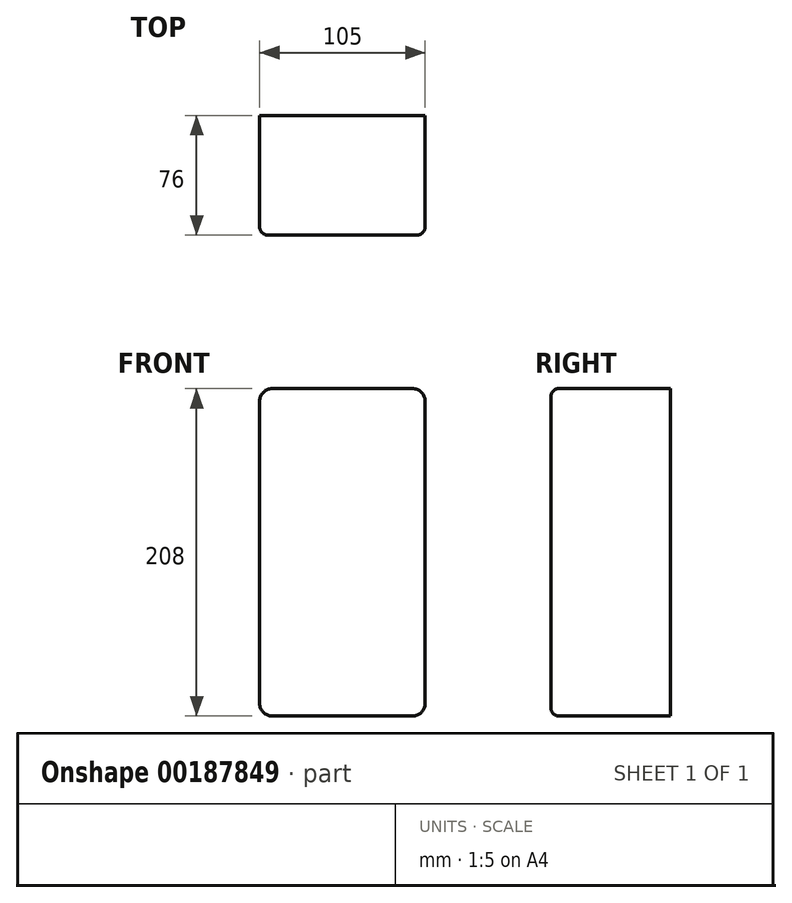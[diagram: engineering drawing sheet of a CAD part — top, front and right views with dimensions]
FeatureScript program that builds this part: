
annotation { "Feature Type Name" : "Feature", "Feature Type Description" : "" }
export const myFeature = defineFeature(function(context is Context, id is Id, definition is map)
    precondition{}
    {
        {
            var Q0;
            Q0=qCreatedBy(makeId("Front.planeOp"),FACE);
            var sketch = newSketch(context, id + "F0", { "sketchPlane" : qUnion([Q0])});
            skLineSegment(sketch, "E0.bottom", {"start": v(-13.11, 91.26) * mm, "end": v(75.89, 91.26) * mm});
            skLineSegment(sketch, "E0.top", {"start": v(-13.11, -116.74) * mm, "end": v(75.89, -116.74) * mm});
            skLineSegment(sketch, "E0.left", {"start": v(-21.11, 83.26) * mm, "end": v(-21.11, -108.74) * mm});
            skLineSegment(sketch, "E0.right", {"start": v(83.89, 83.26) * mm, "end": v(83.89, -108.74) * mm});
            skPoint(sketch, "E1.visualSharp", {"position": v(83.89, 91.26) * mm});
            skArc(sketch, "E1.filletArc", {"start": v(83.89, 83.26) * mm, "mid": v(81.54, 88.91) * mm, "end": v(75.89, 91.26) * mm});
            skPoint(sketch, "E2.visualSharp", {"position": v(-21.11, 91.26) * mm});
            skArc(sketch, "E2.filletArc", {"start": v(-13.11, 91.26) * mm, "mid": v(-18.77, 88.91) * mm, "end": v(-21.11, 83.26) * mm});
            skPoint(sketch, "E3.visualSharp", {"position": v(-21.11, -116.74) * mm});
            skArc(sketch, "E3.filletArc", {"start": v(-21.11, -108.74) * mm, "mid": v(-18.77, -114.4) * mm, "end": v(-13.11, -116.74) * mm});
            skPoint(sketch, "E4.visualSharp", {"position": v(83.89, -116.74) * mm});
            skArc(sketch, "E4.filletArc", {"start": v(75.89, -116.74) * mm, "mid": v(81.54, -114.4) * mm, "end": v(83.89, -108.74) * mm});
            skSolve(sketch);
        }
        {
            var Q0;
            Q0=makeQuery(id+"F0.imprint","IMPRINT",FACE,{"disambiguationData":[TD([[makeQuery(id+"F0.imprint","IMPRINT",EDGE,{"derivedFrom":sQuery(id+"F0.wireOp",EDGE,"E0.bottom")}),-1.0]])]});
            extrude(context, id + "F1", {"entities" : qUnion([Q0]), "depth" : 76 * mm});
        }
        {
            var Q0;
            Q0=makeQuery(id+"F1.opExtrude","CAP_EDGE",EDGE,{"disambiguationData":[OSD([sQuery(id+"F0.wireOp",EDGE,"E0.left")])],"isStart":false});
            fillet(context, id + "F2", {"entities" : qUnion([Q0]), "radius" : 5 * mm, "tangentPropagation" : true, "allowEdgeOverflow" : false});
        }
    });
